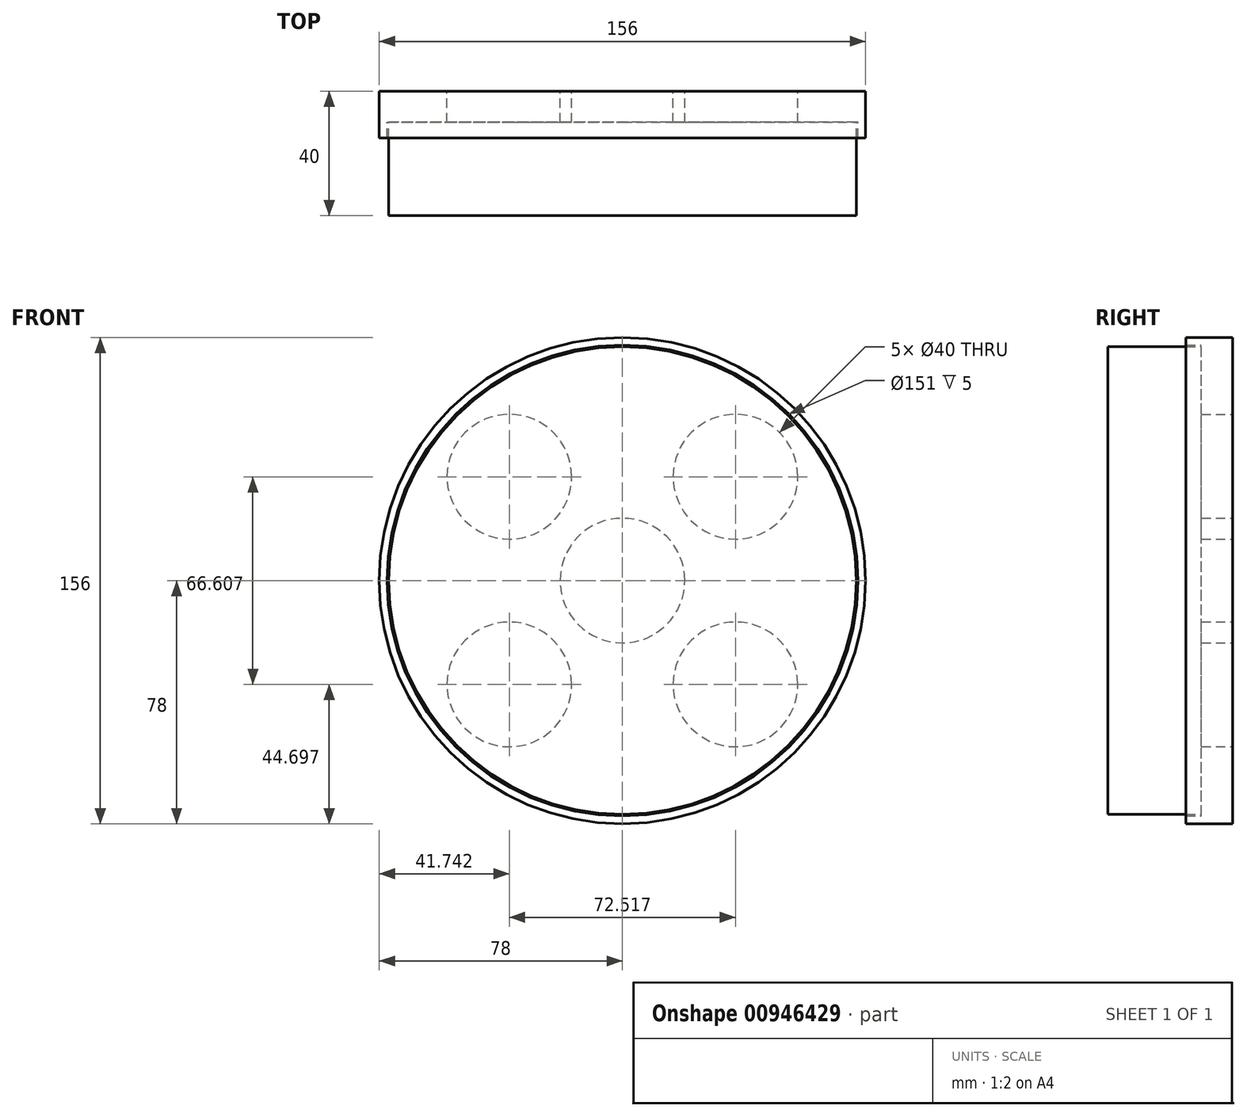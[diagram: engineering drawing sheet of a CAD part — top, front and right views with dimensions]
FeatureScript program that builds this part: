
annotation { "Feature Type Name" : "Feature", "Feature Type Description" : "" }
export const myFeature = defineFeature(function(context is Context, id is Id, definition is map)
    precondition{}
    {
        {
            var Q0;
            Q0=qCreatedBy(makeId("Front.planeOp"),FACE);
            var sketch = newSketch(context, id + "F0", { "sketchPlane" : qUnion([Q0])});
            skCircle(sketch, "E0", {"center": v(0, 0) * mm, "radius": 78 * mm});
            skCircle(sketch, "E1", {"center": v(0, 0) * mm, "radius": 20 * mm});
            skCircle(sketch, "E2", {"center": v(-36.26, 33.3) * mm, "radius": 20 * mm});
            skCircle(sketch, "E3", {"center": v(36.26, 33.3) * mm, "radius": 20 * mm});
            skCircle(sketch, "E4", {"center": v(36.26, -33.3) * mm, "radius": 20 * mm});
            skCircle(sketch, "E5", {"center": v(-36.26, -33.3) * mm, "radius": 20 * mm});
            skCircle(sketch, "E6", {"center": v(0, 0) * mm, "radius": 75.5 * mm});
            skSolve(sketch);
        }
        {
            var Q0;
            Q0=makeQuery(id+"F0.imprint","IMPRINT",FACE,{"disambiguationData":[TD([[makeQuery(id+"F0.imprint","IMPRINT",EDGE,{"derivedFrom":sQuery(id+"F0.wireOp",EDGE,"E1")}),-1.0]])]});
            extrude(context, id + "F1", {"entities" : qUnion([Q0]), "depth" : 10 * mm, "offsetDistance" : 25.4 * mm});
        }
        {
            var Q0;
            Q0=makeQuery(id+"F0.imprint","IMPRINT",FACE,{"disambiguationData":[TD([[makeQuery(id+"F0.imprint","IMPRINT",EDGE,{"derivedFrom":sQuery(id+"F0.wireOp",EDGE,"E0")}),1.0]])]});
            extrude(context, id + "F2", {"entities" : qUnion([Q0]), "operationType" : NewBodyOperationType.ADD, "depth" : 15 * mm, "offsetDistance" : 25.4 * mm});
        }
        {
            var Q0;
            Q0=makeQuery(id+"F1.opExtrude","CAP_FACE",FACE,{"disambiguationData":[OSD([sQuery(id+"F0.wireOp",EDGE,"E1"),sQuery(id+"F0.wireOp",EDGE,"E2"),sQuery(id+"F0.wireOp",EDGE,"E3"),sQuery(id+"F0.wireOp",EDGE,"E4"),sQuery(id+"F0.wireOp",EDGE,"E5"),sQuery(id+"F0.wireOp",EDGE,"E6")])],"isStart":false});
            var sketch = newSketch(context, id + "F3", { "sketchPlane" : qUnion([Q0])});
            skCircle(sketch, "E7", {"center": v(0, 0) * mm, "radius": 75 * mm});
            skSolve(sketch);
        }
        {
            var Q0;
            Q0=makeQuery(id+"F3.imprint","IMPRINT",FACE,{"disambiguationData":[TD([[makeQuery(id+"F3.imprint","IMPRINT",EDGE,{"derivedFrom":makeQuery(id+"F1.opExtrude","CAP_EDGE",EDGE,{"disambiguationData":[OSD([sQuery(id+"F0.wireOp",EDGE,"E3")])],"isStart":false})}),1.0]])]});
            var Q1;
            Q1=makeQuery(id+"F3.imprint","IMPRINT",FACE,{"disambiguationData":[TD([[makeQuery(id+"F3.imprint","IMPRINT",EDGE,{"derivedFrom":makeQuery(id+"F1.opExtrude","CAP_EDGE",EDGE,{"disambiguationData":[OSD([sQuery(id+"F0.wireOp",EDGE,"E2")])],"isStart":false})}),1.0]])]});
            var Q2;
            Q2=makeQuery(id+"F3.imprint","IMPRINT",FACE,{"disambiguationData":[TD([[makeQuery(id+"F3.imprint","IMPRINT",EDGE,{"derivedFrom":makeQuery(id+"F1.opExtrude","CAP_EDGE",EDGE,{"disambiguationData":[OSD([sQuery(id+"F0.wireOp",EDGE,"E5")])],"isStart":false})}),1.0]])]});
            var Q3;
            Q3=makeQuery(id+"F3.imprint","IMPRINT",FACE,{"disambiguationData":[TD([[makeQuery(id+"F3.imprint","IMPRINT",EDGE,{"derivedFrom":sQuery(id+"F3.wireOp",EDGE,"E7")}),1.0]])]});
            var Q4;
            Q4=makeQuery(id+"F3.imprint","IMPRINT",FACE,{"disambiguationData":[TD([[makeQuery(id+"F3.imprint","IMPRINT",EDGE,{"derivedFrom":makeQuery(id+"F1.opExtrude","CAP_EDGE",EDGE,{"disambiguationData":[OSD([sQuery(id+"F0.wireOp",EDGE,"E4")])],"isStart":false})}),1.0]])]});
            var Q5;
            Q5=makeQuery(id+"F3.imprint","IMPRINT",FACE,{"disambiguationData":[TD([[makeQuery(id+"F3.imprint","IMPRINT",EDGE,{"derivedFrom":makeQuery(id+"F1.opExtrude","CAP_EDGE",EDGE,{"disambiguationData":[OSD([sQuery(id+"F0.wireOp",EDGE,"E1")])],"isStart":false})}),1.0]])]});
            var Q6;
            Q6=sQuery(id+"F3.wireOp",EDGE,"E7");
            extrude(context, id + "F4", {"entities" : qUnion([Q0, Q1, Q2, Q3, Q4, Q5]), "surfaceEntities" : qUnion([Q6]), "depth" : 30 * mm, "offsetDistance" : 25.4 * mm});
        }
    });
